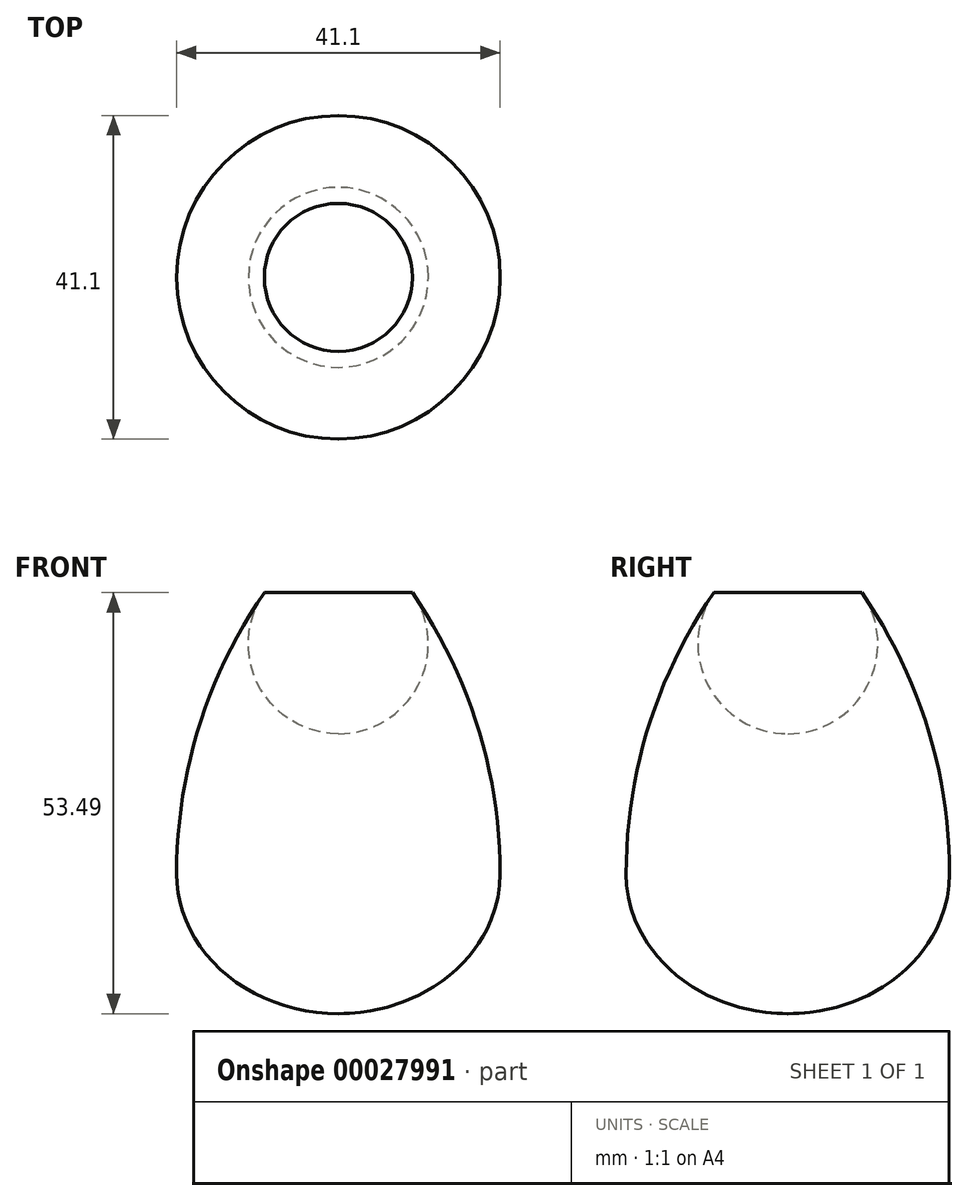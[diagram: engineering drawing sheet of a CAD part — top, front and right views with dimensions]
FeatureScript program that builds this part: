
annotation { "Feature Type Name" : "Feature", "Feature Type Description" : "" }
export const myFeature = defineFeature(function(context is Context, id is Id, definition is map)
    precondition{}
    {
        {
            var Q0;
            Q0=qCreatedBy(makeId("Front.planeOp"),FACE);
            var sketch = newSketch(context, id + "F0", { "sketchPlane" : qUnion([Q0])});
            skEllipse(sketch, "E0", {"center": v(0, 0) * mm, "majorRadius": 17.78 * mm, "minorRadius": 20.55 * mm, "majorAxis": v(0, 1)});
            skCircle(sketch, "E1", {"center": v(0, 29.21) * mm, "radius": 11.43 * mm});
            skArc(sketch, "E2", {"start": v(-9.4, 35.71) * mm, "mid": v(-17.7, 18.7) * mm, "end": v(-20.55, 0) * mm});
            skLineSegment(sketch, "E3", {"start": v(0, 29.21) * mm, "end": v(0, 0) * mm});
            skArc(sketch, "E4", {"start": v(20.55, 0) * mm, "mid": v(17.7, 18.7) * mm, "end": v(9.4, 35.71) * mm});
            skLineSegment(sketch, "E5", {"start": v(0, 29.21) * mm, "end": v(0, 40.64) * mm});
            skLineSegment(sketch, "E6", {"start": v(0, 40.64) * mm, "end": v(0, -17.78) * mm});
            skSolve(sketch);
        }
        {
            var Q0;
            {var subQ0=sQuery(id+"F0.wireOp",EDGE,"E2");Q0=makeQuery(id+"F0.imprint","IMPRINT",FACE,{"disambiguationData":[TD([[makeQuery(id+"F0.imprint","IMPRINT",EDGE,{"derivedFrom":subQ0}),1.0]])]});}
            var Q1;
            {var subQ0=sQuery(id+"F0.wireOp",EDGE,"E6");var subQ3=makeQuery(id+"F0.imprint","IMPRINT",VERTEX,{"disambiguationData":[OD(0.0)],"derivedFrom":subQ0});Q1=makeQuery(id+"F0.imprint","IMPRINT",FACE,{"disambiguationData":[TD([[makeQuery(id+"F0.imprint","IMPRINT",EDGE,{"disambiguationData":[TD([[subQ3,1.0]])],"derivedFrom":subQ0}),-1.0]])]});}
            var Q2;
            {var subQ0=sQuery(id+"F0.wireOp",EDGE,"E6");var subQ1=makeQuery(id+"F0.imprint","IMPRINT",VERTEX,{"disambiguationData":[OD(1.0)],"derivedFrom":subQ0});Q2=makeQuery(id+"F0.imprint","IMPRINT",FACE,{"disambiguationData":[TD([[makeQuery(id+"F0.imprint","IMPRINT",EDGE,{"disambiguationData":[TD([[subQ1,-1.0]])],"derivedFrom":subQ0}),-1.0]])]});}
            var Q3;
            Q3=sQuery(id+"F0.wireOp",EDGE,"E6");
            revolve(context, id + "F1", {"entities" : qUnion([Q0, Q1, Q2]), "axis" : qUnion([Q3]), "revolveType" : RevolveType.FULL});
        }
    });
